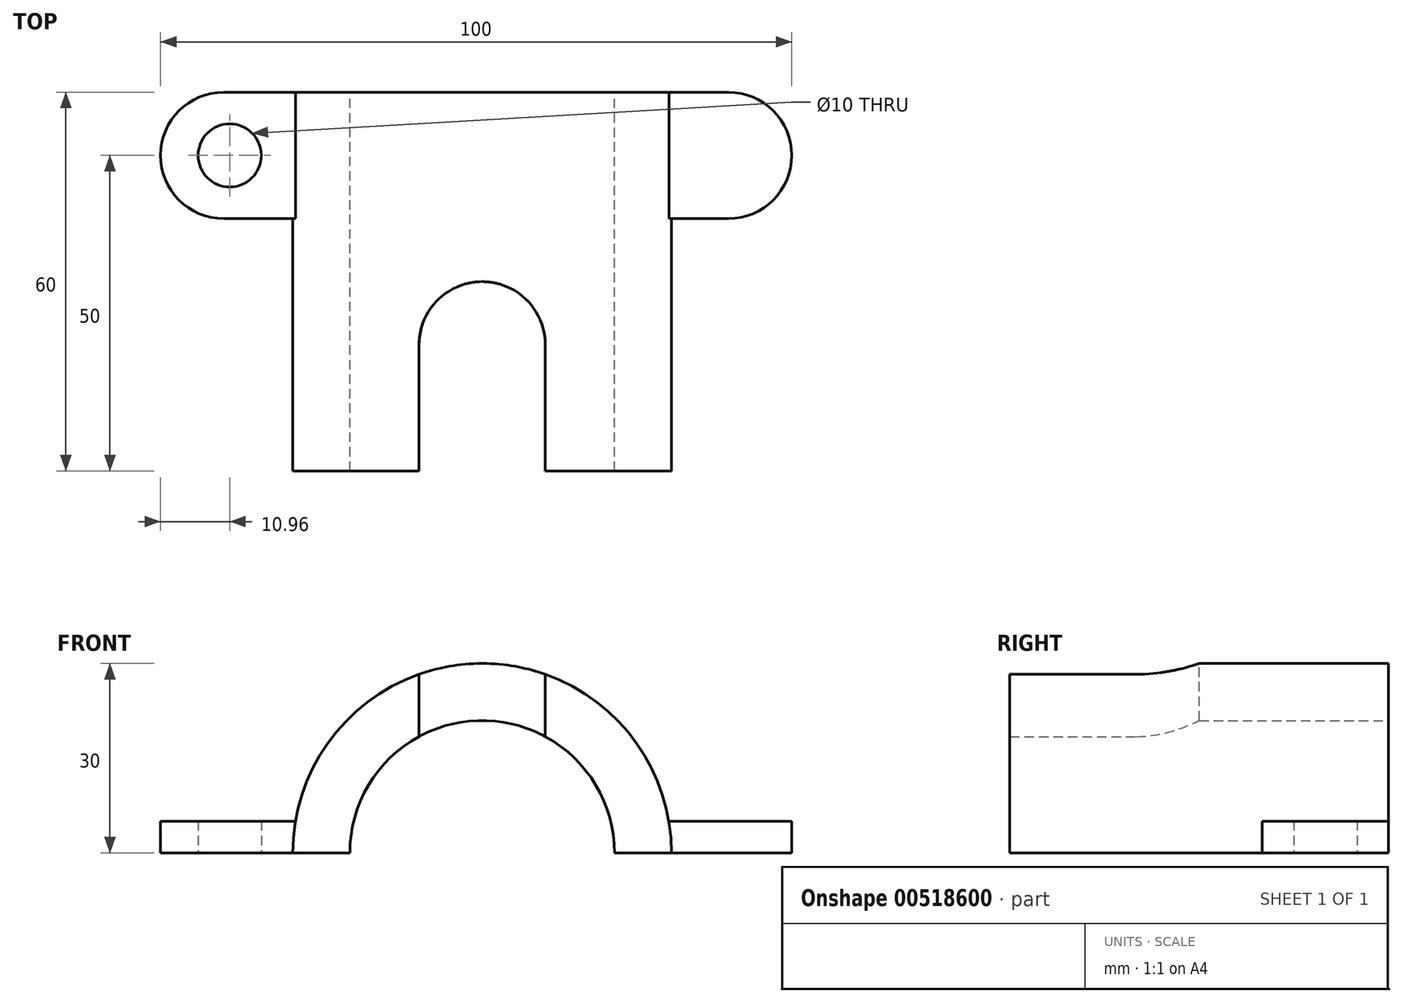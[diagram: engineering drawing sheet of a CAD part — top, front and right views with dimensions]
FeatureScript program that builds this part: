
annotation { "Feature Type Name" : "Feature", "Feature Type Description" : "" }
export const myFeature = defineFeature(function(context is Context, id is Id, definition is map)
    precondition{}
    {
        {
            assignVariable(context, id + "F0", {"name" : "A", "anyValue" : 5});
        }
        {
            var Q0;
            Q0=qCreatedBy(makeId("Top.planeOp"),FACE);
            var sketch = newSketch(context, id + "F1", { "sketchPlane" : qUnion([Q0])});
            skLineSegment(sketch, "E0.bottom", {"start": v(0, 0) * mm, "end": v(30, 0) * mm});
            skLineSegment(sketch, "E0.top", {"start": v(0, 60) * mm, "end": v(30, 60) * mm});
            skLineSegment(sketch, "E0.left", {"start": v(0, 0) * mm, "end": v(0, 60) * mm});
            skLineSegment(sketch, "E0.right", {"start": v(30, 0) * mm, "end": v(30, 60) * mm});
            skSolve(sketch);
        }
        {
            var Q0;
            Q0=makeQuery(id+"F1.imprint","IMPRINT",FACE,{"disambiguationData":[TD([[makeQuery(id+"F1.imprint","IMPRINT",EDGE,{"derivedFrom":sQuery(id+"F1.wireOp",EDGE,"E0.bottom")}),1.0]])]});
            var Q1;
            Q1=sQuery(id+"F1.wireOp",EDGE,"E0.left");
            revolve(context, id + "F2", {"entities" : qUnion([Q0]), "axis" : qUnion([Q1]), "revolveType" : RevolveType.ONE_DIRECTION, "oppositeDirection" : true, "angle" : 180 * degree});
        }
        {
            var Q0;
            Q0=qCreatedBy(makeId("Top.planeOp"),FACE);
            var sketch = newSketch(context, id + "F3", { "sketchPlane" : qUnion([Q0])});
            skLineSegment(sketch, "E1.bottom", {"start": v(-50.96, 60) * mm, "end": v(49.04, 60) * mm});
            skLineSegment(sketch, "E1.top", {"start": v(-50.96, 40) * mm, "end": v(49.04, 40) * mm});
            skLineSegment(sketch, "E1.left", {"start": v(-50.96, 60) * mm, "end": v(-50.96, 40) * mm});
            skLineSegment(sketch, "E1.right", {"start": v(49.04, 60) * mm, "end": v(49.04, 40) * mm});
            skSolve(sketch);
        }
        {
            var Q0;
            Q0 = qSketchRegion(id + "F3", true);
            extrude(context, id + "F4", {"entities" : qUnion([Q0]), "operationType" : NewBodyOperationType.ADD, "depth" : (getVariable(context, 'A')) * mm, "offsetDistance" : 25 * mm});
        }
        {
            var Q0;
            Q0=makeQuery(id+"F4.opExtrude","SWEPT_EDGE",EDGE,{"disambiguationData":[OSD([sQuery(id+"F3.wireOp",EDGE,"E1.bottom"),sQuery(id+"F3.wireOp",EDGE,"E1.left")])]});
            var Q1;
            Q1=makeQuery(id+"F4.opExtrude","SWEPT_EDGE",EDGE,{"disambiguationData":[OSD([sQuery(id+"F3.wireOp",EDGE,"E1.top"),sQuery(id+"F3.wireOp",EDGE,"E1.left")])]});
            var Q2;
            Q2=makeQuery(id+"F4.opExtrude","SWEPT_EDGE",EDGE,{"disambiguationData":[OSD([sQuery(id+"F3.wireOp",EDGE,"E1.top"),sQuery(id+"F3.wireOp",EDGE,"E1.right")])]});
            var Q3;
            Q3=makeQuery(id+"F4.opExtrude","SWEPT_EDGE",EDGE,{"disambiguationData":[OSD([sQuery(id+"F3.wireOp",EDGE,"E1.bottom"),sQuery(id+"F3.wireOp",EDGE,"E1.right")])]});
            fillet(context, id + "F5", {"entities" : qUnion([Q0, Q1, Q2, Q3]), "radius" : 10 * mm, "tangentPropagation" : true, "allowEdgeOverflow" : false});
        }
        {
            var Q0;
            Q0=qCreatedBy(makeId("Top.planeOp"),FACE);
            var sketch = newSketch(context, id + "F6", { "sketchPlane" : qUnion([Q0])});
            skLineSegment(sketch, "E2", {"start": v(0, 64.4) * mm, "end": v(0, 36.22) * mm, "construction": true});
            skCircle(sketch, "E3", {"center": v(-40, 50) * mm, "radius": 5 * mm});
            skCircle(sketch, "E4.MirrorC", {"center": v(40, 50) * mm, "radius": 5 * mm});
            skSolve(sketch);
        }
        {
            var Q0;
            Q0=makeQuery(id+"F6.imprint","IMPRINT",FACE,{"disambiguationData":[TD([[makeQuery(id+"F6.imprint","IMPRINT",EDGE,{"derivedFrom":sQuery(id+"F6.wireOp",EDGE,"E4.MirrorC")}),-1.0]])]});
            var Q1;
            Q1=makeQuery(id+"F6.imprint","IMPRINT",FACE,{"disambiguationData":[TD([[makeQuery(id+"F6.imprint","IMPRINT",EDGE,{"derivedFrom":sQuery(id+"F6.wireOp",EDGE,"E3")}),1.0]])]});
            extrude(context, id + "F7", {"entities" : qUnion([Q0, Q1]), "operationType" : NewBodyOperationType.REMOVE, "endBound" : BoundingType.THROUGH_ALL, "depth" : 25 * mm, "offsetDistance" : 25 * mm});
        }
        {
            var Q0;
            Q0=qCreatedBy(makeId("Top.planeOp"),FACE);
            var sketch = newSketch(context, id + "F8", { "sketchPlane" : qUnion([Q0])});
            skLineSegment(sketch, "E5.bottom", {"start": v(-10, 0) * mm, "end": v(10, 0) * mm});
            skLineSegment(sketch, "E5.top", {"start": v(-10, 30) * mm, "end": v(10, 30) * mm});
            skLineSegment(sketch, "E5.left", {"start": v(-10, 0) * mm, "end": v(-10, 30) * mm});
            skLineSegment(sketch, "E5.right", {"start": v(10, 0) * mm, "end": v(10, 30) * mm});
            skSolve(sketch);
        }
        {
            var Q0;
            Q0 = qSketchRegion(id + "F8", true);
            extrude(context, id + "F9", {"entities" : qUnion([Q0]), "operationType" : NewBodyOperationType.REMOVE, "endBound" : BoundingType.THROUGH_ALL, "depth" : 25 * mm, "offsetDistance" : 25 * mm});
        }
        {
            var Q0;
            Q0=makeQuery(id+"F9.boolean.opBoolean","COPY",EDGE,{"derivedFrom":makeQuery(id+"F9.opExtrude","SWEPT_EDGE",EDGE,{"disambiguationData":[OSD([sQuery(id+"F8.wireOp",EDGE,"E5.top"),sQuery(id+"F8.wireOp",EDGE,"E5.left")])]})});
            var Q1;
            Q1=makeQuery(id+"F9.boolean.opBoolean","COPY",EDGE,{"derivedFrom":makeQuery(id+"F9.opExtrude","SWEPT_EDGE",EDGE,{"disambiguationData":[OSD([sQuery(id+"F8.wireOp",EDGE,"E5.top"),sQuery(id+"F8.wireOp",EDGE,"E5.right")])]})});
            fillet(context, id + "F10", {"entities" : qUnion([Q0, Q1]), "radius" : 10 * mm, "tangentPropagation" : true, "allowEdgeOverflow" : false});
        }
        {
            var Q0;
            Q0=makeQuery(id+"F4.boolean.opBoolean","MERGE",FACE,{"derivedFrom":[makeQuery(id+"F2.opRevolve","SWEPT_FACE",FACE,{"disambiguationData":[OSD([sQuery(id+"F1.wireOp",EDGE,"E0.top")])]}),makeQuery(id+"F4.opExtrude","SWEPT_FACE",FACE,{"disambiguationData":[OSD([sQuery(id+"F3.wireOp",EDGE,"E1.bottom")])]})]});
            var sketch = newSketch(context, id + "F11", { "sketchPlane" : qUnion([Q0])});
            skCircle(sketch, "E6", {"center": v(0, 0) * mm, "radius": 20.96 * mm});
            skSolve(sketch);
        }
        {
            var Q0;
            Q0 = qSketchRegion(id + "F11", true);
            extrude(context, id + "F12", {"entities" : qUnion([Q0]), "operationType" : NewBodyOperationType.REMOVE, "endBound" : BoundingType.THROUGH_ALL, "oppositeDirection" : true, "depth" : 25 * mm, "offsetDistance" : 25 * mm});
        }
    });
